# Revit family: PRD_AR_WstBins_WasteBin_BS610
name_source: partatom
category: Furniture
revit_build: Autodesk Revit 2018 (Build: 20190510_1515(x64)
units: mm (PartAtom-declared; Revit-internal decimal feet)

## family parameters
Cut with Voids When Loaded = No
Host = Face
OmniClass Number = 23.40.20.31.11
OmniClass Title = Bins
Room Calculation Point = No
Shared = No

## types (1)
- BS610
    AssetType = Fixed
    BIMObjectName = PRD_AR_WasteBins_WasteBin_BS610
    Category = Pr_40_50_07_96, Waste bins
    Color = Stainless steel
    Default Elevation = 820 mm  [stored 2.69029 ft]
    Description = Waste bin for wall mounting, stainless steel, surface satin finished, material thickness 1.2 mm, with a 180° radius front and perforated fascia pattern, cylinder lock with KWC standard key, approx. 22 liter capacity, incl. stainless steel screws and dowels.
    DurationUnit = year
    Features = stainless steel, 1.20 mm, satin finished, wall mounting, 410x380x222 mm (WxHxD)
    FillingVolume = 23.00 L
    Finish = Satin finished
    FinishAndColour = Stainless steel, satin finished
    Form = Wall mounted
    GrossWeight = 5.30 kg
    IfcExportAs = IfcFurnitureType
    IfcExportType = NOTDEFINED
    IntegralAccessories = Stainless steel screws and dowels incl.
    Lid = no
    Lock = no
    MainColor = Stainless steel
    Manufacturer = KWC Group AG
    ManufacturerName = KWC Group AG
    ManufacturerURL = www.kwc.com
    Material = Stainless steel
    Materials = Stainless steel 1.4301
    Model = BS610
    ModelNumber = 2000056825
    ModelReference = BS610
    NBSDescription = Waste bins
    NBSReference = 45-35-72/380
    Name = Waste bin BS610
    NetWeight = 4.50 kg
    NominalDepth = 222 mm
    NominalHeight = 380 mm
    NominalLength = 410 mm  [stored 1.34514 ft]
    NominalWidth = 410 mm  [stored 1.34514 ft]
    ProductInformation = https://pim.kwc.com
    Size = 410 x 380 x 222 mm
    Style = Waste bin
    URL = www.kwc.com
    Uniclass2015Code = Pr_40_50_07_96
    Uniclass2015Title = Waste bins
    Uniclass2015Version = Products v1.5
    Version = 1
    WarrantyDurationUnit = year
    WasteBinMaterial = PRD_AR_StainlessSteel_SatinFinished
    WasteBinPerforationMaterial = PRD_AR_StainlessSteel_SatinFinished_Perforated

note: [stored X ft] marks values corroborated as IEEE doubles in the binary element streams (Revit-internal decimal feet)

## geometry (parser evidence)
native form markers: Sweep x2
no freeform markers — native parametric forms only
